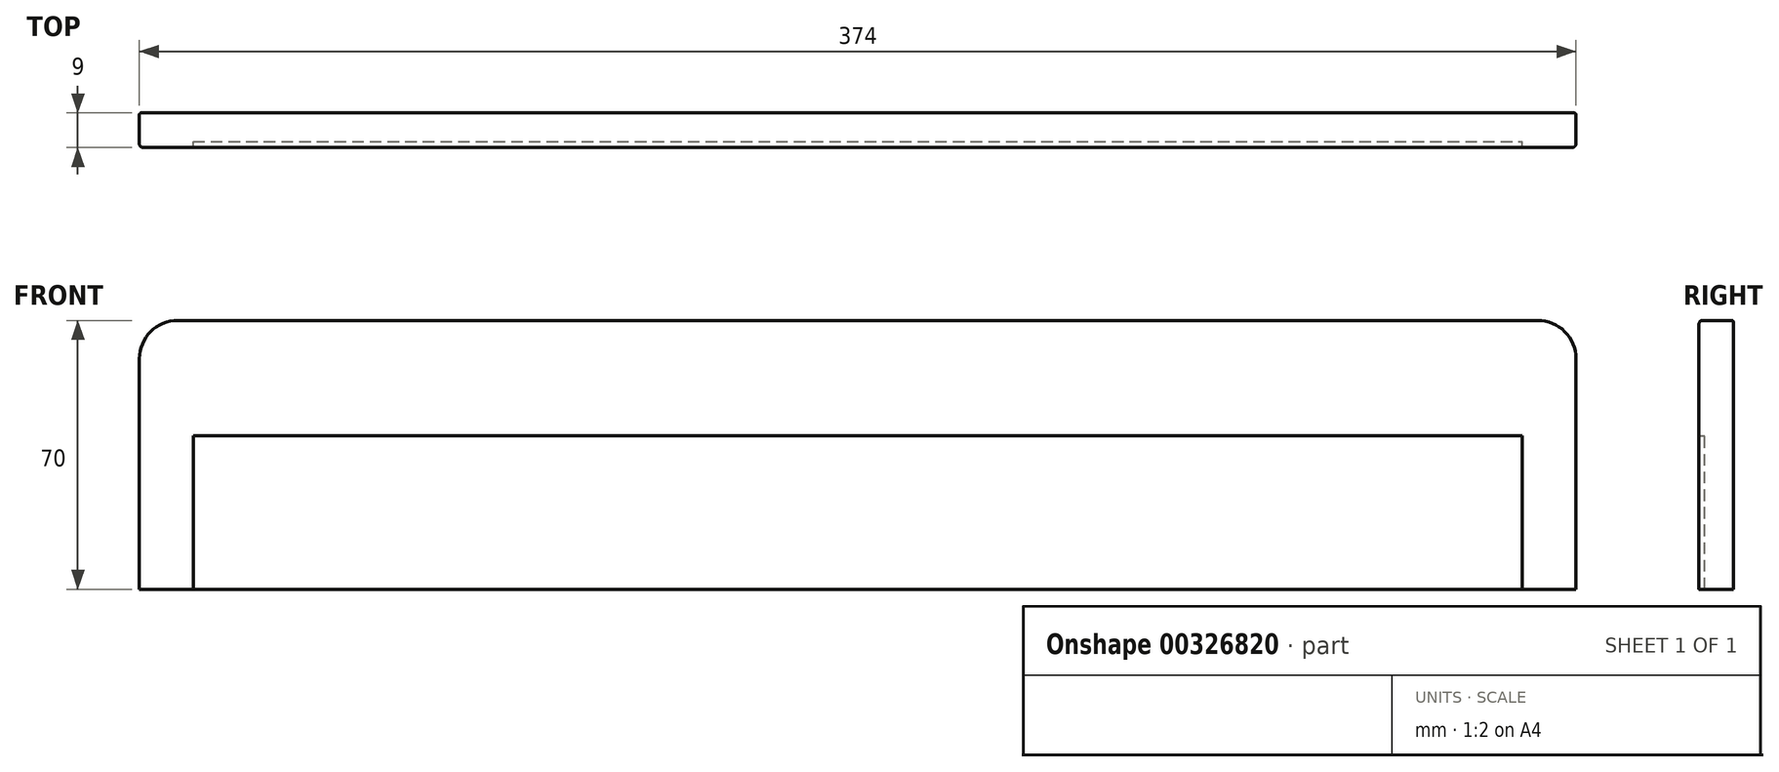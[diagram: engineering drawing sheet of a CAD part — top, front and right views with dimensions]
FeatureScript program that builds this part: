
annotation { "Feature Type Name" : "Feature", "Feature Type Description" : "" }
export const myFeature = defineFeature(function(context is Context, id is Id, definition is map)
    precondition{}
    {
        {
            var Q0;
            Q0=qCreatedBy(makeId("Front.planeOp"),FACE);
            var sketch = newSketch(context, id + "F0", { "sketchPlane" : qUnion([Q0])});
            skLineSegment(sketch, "E0.bottom", {"start": v(-49.72, 31.18) * mm, "end": v(137.28, 31.18) * mm});
            skLineSegment(sketch, "E0.top", {"start": v(-49.72, -38.82) * mm, "end": v(137.28, -38.82) * mm});
            skLineSegment(sketch, "E0.left", {"start": v(-49.72, 31.18) * mm, "end": v(-49.72, -38.82) * mm});
            skLineSegment(sketch, "E0.right", {"start": v(137.28, 31.18) * mm, "end": v(137.28, -38.82) * mm});
            skLineSegment(sketch, "E1.bottom", {"start": v(137.28, -38.82) * mm, "end": v(-35.72, -38.82) * mm});
            skLineSegment(sketch, "E1.top", {"start": v(137.28, 1.18) * mm, "end": v(-35.72, 1.18) * mm});
            skLineSegment(sketch, "E1.left", {"start": v(137.28, -38.82) * mm, "end": v(137.28, 1.18) * mm});
            skLineSegment(sketch, "E1.right", {"start": v(-35.72, -38.82) * mm, "end": v(-35.72, 1.18) * mm});
            skSolve(sketch);
        }
        {
            var Q0;
            Q0=makeQuery(id+"F0.imprint","IMPRINT",FACE,{"disambiguationData":[TD([[makeQuery(id+"F0.imprint","IMPRINT",EDGE,{"derivedFrom":sQuery(id+"F0.wireOp",EDGE,"E0.bottom")}),-1.0]])]});
            extrude(context, id + "F1", {"entities" : qUnion([Q0]), "depth" : 9 * mm});
        }
        {
            var Q0;
            Q0 = qSketchRegion(id + "F0", true);
            extrude(context, id + "F2", {"entities" : qUnion([Q0]), "operationType" : NewBodyOperationType.ADD, "depth" : 7.5 * mm});
        }
        {
            var Q0;
            Q0=makeQuery(id+"F1.opExtrude","SWEPT_EDGE",EDGE,{"disambiguationData":[OSD([sQuery(id+"F0.wireOp",EDGE,"E0.bottom"),sQuery(id+"F0.wireOp",EDGE,"E0.left")])]});
            fillet(context, id + "F3", {"entities" : qUnion([Q0]), "radius" : 10 * mm, "tangentPropagation" : true, "allowEdgeOverflow" : false});
        }
        {
            var Q0;
            Q0=makeQuery(id+"F1.opExtrude","CAP_EDGE",EDGE,{"disambiguationData":[OSD([sQuery(id+"F0.wireOp",EDGE,"E0.bottom")])],"isStart":false});
            var Q1;
            {var subQ0=sQuery(id+"F0.wireOp",EDGE,"E0.left");var subQ1=sQuery(id+"F0.wireOp",EDGE,"E0.bottom");Q1=makeQuery(id+"F3.opFillet","BLEND_EDGE",EDGE,{"blendedFrom":[makeQuery(id+"F1.opExtrude","SWEPT_EDGE",EDGE,{"disambiguationData":[OSD([subQ1,subQ0])]}),makeQuery(id+"F1.opExtrude","CAP_FACE",FACE,{"disambiguationData":[OSD([subQ1,sQuery(id+"F0.wireOp",EDGE,"E0.top"),subQ0,sQuery(id+"F0.wireOp",EDGE,"E0.right"),sQuery(id+"F0.wireOp",EDGE,"E1.top"),sQuery(id+"F0.wireOp",EDGE,"E1.right")])],"isStart":false})],"blendedInto":[makeQuery(id+"F1.opExtrude","CAP_FACE",FACE,{"disambiguationData":[OSD([subQ1,sQuery(id+"F0.wireOp",EDGE,"E0.top"),subQ0,sQuery(id+"F0.wireOp",EDGE,"E0.right"),sQuery(id+"F0.wireOp",EDGE,"E1.top"),sQuery(id+"F0.wireOp",EDGE,"E1.right")])],"isStart":false})]});}
            var Q2;
            Q2=makeQuery(id+"F1.opExtrude","CAP_EDGE",EDGE,{"disambiguationData":[OSD([sQuery(id+"F0.wireOp",EDGE,"E0.left")])],"isStart":false});
            fillet(context, id + "F4", {"entities" : qUnion([Q0, Q1, Q2]), "radius" : 1 * mm, "tangentPropagation" : true, "allowEdgeOverflow" : false});
        }
        {
            var Q0;
            Q0=makeQuery(id+"F1.opExtrude","CAP_EDGE",EDGE,{"disambiguationData":[OSD([sQuery(id+"F0.wireOp",EDGE,"E0.bottom")])],"isStart":true});
            var Q1;
            {var subQ0=sQuery(id+"F0.wireOp",EDGE,"E0.right");var subQ1=sQuery(id+"F0.wireOp",EDGE,"E0.left");var subQ2=sQuery(id+"F0.wireOp",EDGE,"E0.top");var subQ3=sQuery(id+"F0.wireOp",EDGE,"E0.bottom");Q1=makeQuery(id+"F3.opFillet","BLEND_EDGE",EDGE,{"blendedFrom":[makeQuery(id+"F1.opExtrude","SWEPT_EDGE",EDGE,{"disambiguationData":[OSD([subQ3,subQ1])]}),makeQuery(id+"F2.boolean.opBoolean","MERGE",FACE,{"derivedFrom":[makeQuery(id+"F1.opExtrude","CAP_FACE",FACE,{"disambiguationData":[OSD([subQ3,subQ2,subQ1,subQ0,sQuery(id+"F0.wireOp",EDGE,"E1.top"),sQuery(id+"F0.wireOp",EDGE,"E1.right")])],"isStart":true}),makeQuery(id+"F2.opExtrude","CAP_FACE",FACE,{"disambiguationData":[OSD([subQ3,subQ2,subQ1,subQ0,sQuery(id+"F0.wireOp",EDGE,"E1.bottom"),sQuery(id+"F0.wireOp",EDGE,"E1.left")])],"isStart":true})]})],"blendedInto":[makeQuery(id+"F2.boolean.opBoolean","MERGE",FACE,{"derivedFrom":[makeQuery(id+"F1.opExtrude","CAP_FACE",FACE,{"disambiguationData":[OSD([subQ3,subQ2,subQ1,subQ0,sQuery(id+"F0.wireOp",EDGE,"E1.top"),sQuery(id+"F0.wireOp",EDGE,"E1.right")])],"isStart":true}),makeQuery(id+"F2.opExtrude","CAP_FACE",FACE,{"disambiguationData":[OSD([subQ3,subQ2,subQ1,subQ0,sQuery(id+"F0.wireOp",EDGE,"E1.bottom"),sQuery(id+"F0.wireOp",EDGE,"E1.left")])],"isStart":true})]})]});}
            var Q2;
            Q2=makeQuery(id+"F1.opExtrude","CAP_EDGE",EDGE,{"disambiguationData":[OSD([sQuery(id+"F0.wireOp",EDGE,"E0.left")])],"isStart":true});
            fillet(context, id + "F5", {"entities" : qUnion([Q0, Q1, Q2]), "radius" : 0.5 * mm, "tangentPropagation" : true, "allowEdgeOverflow" : false});
        }
        {
            var Q0;
            Q0=makeQuery(id+"F1.opExtrude","SWEPT_BODY",BODY,{"disambiguationData":[OSD([sQuery(id+"F0.wireOp",EDGE,"E0.bottom"),sQuery(id+"F0.wireOp",EDGE,"E0.top"),sQuery(id+"F0.wireOp",EDGE,"E0.left"),sQuery(id+"F0.wireOp",EDGE,"E0.right"),sQuery(id+"F0.wireOp",EDGE,"E1.top"),sQuery(id+"F0.wireOp",EDGE,"E1.right")])]});
            var Q1;
            {var subQ0=sQuery(id+"F0.wireOp",EDGE,"E0.right");Q1=makeQuery(id+"F2.boolean.opBoolean","MERGE",FACE,{"derivedFrom":[makeQuery(id+"F1.opExtrude","SWEPT_FACE",FACE,{"disambiguationData":[OSD([subQ0])]}),makeQuery(id+"F2.opExtrude","SWEPT_FACE",FACE,{"disambiguationData":[OSD([subQ0,sQuery(id+"F0.wireOp",EDGE,"E1.left")])]})]});}
            mirror(context, id + "F6", {"operationType" : NewBodyOperationType.ADD, "entities" : qUnion([Q0]), "mirrorPlane" : qUnion([Q1])});
        }
    });
